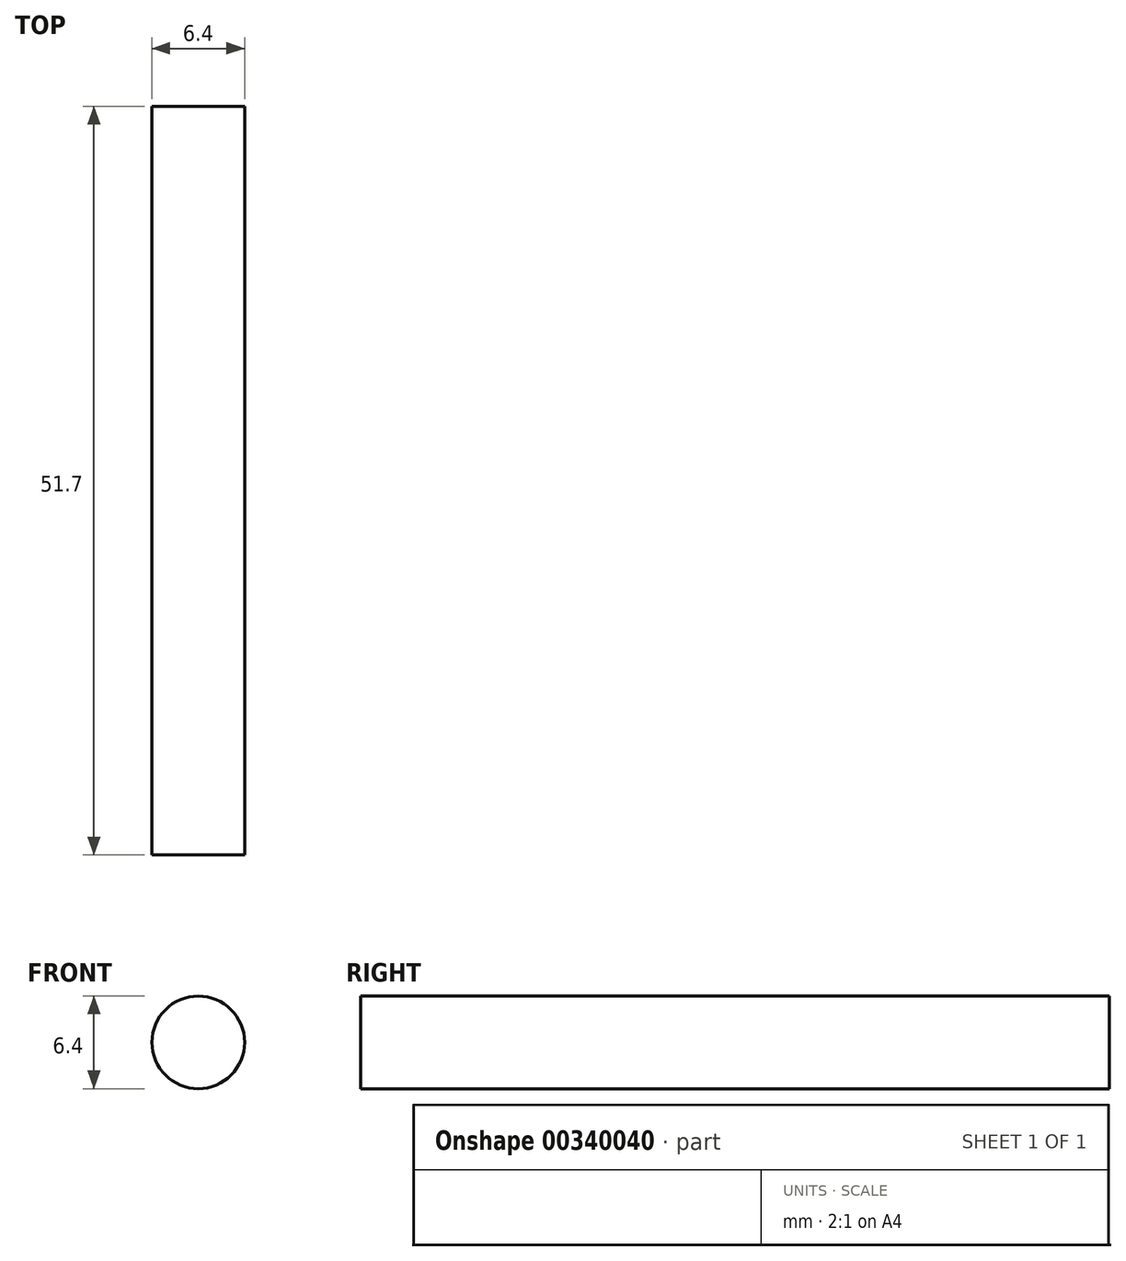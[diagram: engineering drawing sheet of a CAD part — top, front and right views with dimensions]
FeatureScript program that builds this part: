
annotation { "Feature Type Name" : "Feature", "Feature Type Description" : "" }
export const myFeature = defineFeature(function(context is Context, id is Id, definition is map)
    precondition{}
    {
        {
            var Q0;
            Q0=qCreatedBy(makeId("Front.planeOp"),FACE);
            var sketch = newSketch(context, id + "F0", { "sketchPlane" : qUnion([Q0])});
            skCircle(sketch, "E0", {"center": v(0, 0) * mm, "radius": 3.2 * mm});
            skSolve(sketch);
        }
        {
            var Q0;
            Q0 = qSketchRegion(id + "F0", true);
            extrude(context, id + "F1", {"entities" : qUnion([Q0]), "depth" : 51.7 * mm});
        }
    });
